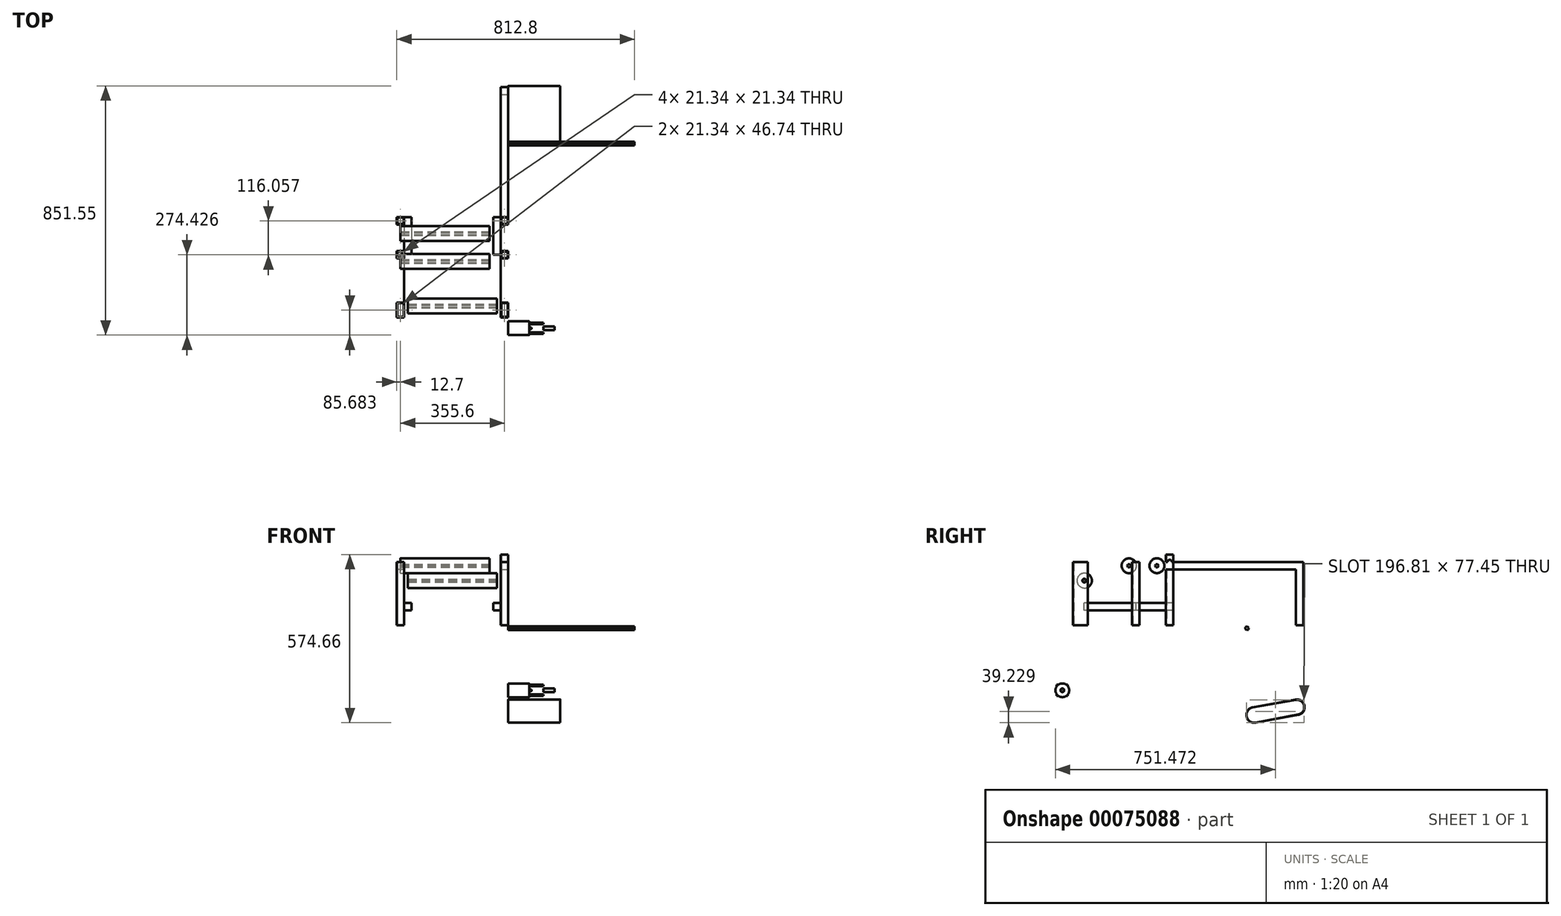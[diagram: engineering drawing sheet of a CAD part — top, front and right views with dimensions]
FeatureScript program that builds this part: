
annotation { "Feature Type Name" : "Feature", "Feature Type Description" : "" }
export const myFeature = defineFeature(function(context is Context, id is Id, definition is map)
    precondition{}
    {
        {
            var Q0;
            Q0=qCreatedBy(makeId("Right.planeOp"),FACE);
            var sketch = newSketch(context, id + "F0", { "sketchPlane" : qUnion([Q0])});
            skLineSegment(sketch, "E0.left", {"start": v(-485.15, -12.17) * mm, "end": v(-485.15, -62.97) * mm, "construction": true});
            skLineSegment(sketch, "E1", {"start": v(-472.45, -12.17) * mm, "end": v(-472.45, 203.73) * mm});
            skLineSegment(sketch, "E2", {"start": v(-472.45, 203.73) * mm, "end": v(-421.65, 203.73) * mm});
            skLineSegment(sketch, "E3", {"start": v(-421.65, 203.73) * mm, "end": v(-421.65, -12.17) * mm});
            skLineSegment(sketch, "E4", {"start": v(-421.65, -12.17) * mm, "end": v(-472.45, -12.17) * mm});
            skLineSegment(sketch, "E5.bottom", {"start": v(-154.95, -12.17) * mm, "end": v(-129.55, -12.17) * mm});
            skLineSegment(sketch, "E5.top", {"start": v(-154.95, 229.13) * mm, "end": v(-129.55, 229.13) * mm});
            skLineSegment(sketch, "E5.left", {"start": v(-154.95, -12.17) * mm, "end": v(-154.95, 229.13) * mm});
            skLineSegment(sketch, "E5.right", {"start": v(-129.55, -12.17) * mm, "end": v(-129.55, 229.13) * mm});
            skLineSegment(sketch, "E6", {"start": v(-283.35, -12.17) * mm, "end": v(-283.35, 178.33) * mm, "construction": true});
            skLineSegment(sketch, "E7.bottom", {"start": v(-421.65, 178.33) * mm, "end": v(-154.95, 178.33) * mm});
            skLineSegment(sketch, "E7.top", {"start": v(-421.65, 203.73) * mm, "end": v(-154.95, 203.73) * mm});
            skLineSegment(sketch, "E7.left", {"start": v(-421.65, 178.33) * mm, "end": v(-421.65, 203.73) * mm});
            skLineSegment(sketch, "E7.right", {"start": v(-154.95, 178.33) * mm, "end": v(-154.95, 203.73) * mm});
            skLineSegment(sketch, "E8", {"start": v(-142.25, -12.17) * mm, "end": v(-142.25, 229.13) * mm, "construction": true});
            skPoint(sketch, "E9.endSnap0", {"position": v(-447.05, -12.17) * mm});
            skCircle(sketch, "E10", {"center": v(-434.35, 140.23) * mm, "radius": 6.35 * mm});
            skLineSegment(sketch, "E11", {"start": v(-421.65, 191.03) * mm, "end": v(-154.95, 191.03) * mm, "construction": true});
            skLineSegment(sketch, "E12", {"start": v(-294.65, 140.23) * mm, "end": v(-294.65, 203.73) * mm, "construction": true});
            skLineSegment(sketch, "E13", {"start": v(-294.65, 191.03) * mm, "end": v(-287.4, 197.2) * mm, "construction": true});
            skCircle(sketch, "E14", {"center": v(-294.65, 191.03) * mm, "radius": 9.52 * mm});
            skLineSegment(sketch, "E15.bottom", {"start": v(-154.95, 203.73) * mm, "end": v(314.95, 203.73) * mm});
            skLineSegment(sketch, "E15.top", {"start": v(-154.95, 178.33) * mm, "end": v(314.95, 178.33) * mm});
            skLineSegment(sketch, "E15.left", {"start": v(-154.95, 203.73) * mm, "end": v(-154.95, 178.33) * mm});
            skLineSegment(sketch, "E15.right", {"start": v(314.95, 203.73) * mm, "end": v(314.95, 178.33) * mm});
            skCircle(sketch, "E16", {"center": v(-142.25, 203.73) * mm, "radius": 7.62 * mm});
            skCircle(sketch, "E17", {"center": v(-212.1, 191.03) * mm, "radius": 7.62 * mm});
            skLineSegment(sketch, "E18.bottom", {"start": v(-271, 203.73) * mm, "end": v(-245.6, 203.73) * mm});
            skLineSegment(sketch, "E18.top", {"start": v(-271, -12.17) * mm, "end": v(-245.6, -12.17) * mm});
            skLineSegment(sketch, "E18.left", {"start": v(-271, 203.73) * mm, "end": v(-271, -12.17) * mm});
            skLineSegment(sketch, "E18.right", {"start": v(-245.6, 203.73) * mm, "end": v(-245.6, -12.17) * mm});
            skLineSegment(sketch, "E19.bottom", {"start": v(314.95, 203.73) * mm, "end": v(289.55, 203.73) * mm});
            skLineSegment(sketch, "E19.top", {"start": v(314.95, -12.17) * mm, "end": v(289.55, -12.17) * mm});
            skLineSegment(sketch, "E19.left", {"start": v(314.95, 203.73) * mm, "end": v(314.95, -12.17) * mm});
            skLineSegment(sketch, "E19.right", {"start": v(289.55, 203.73) * mm, "end": v(289.55, -12.17) * mm});
            skSolve(sketch);
        }
        {
            var Q0;
            Q0=qCreatedBy(makeId("Right.planeOp"),FACE);
            var Q1;
            Q1=qBodyType(qCreatedBy(id+"F2",EDGE),BodyType.WIRE);
            cPlane(context, id + "F1", {"entities" : qUnion([Q0, Q1]), "cplaneType" : CPlaneType.OFFSET, "offset" : 63.5 * mm, "oppositeDirection" : true, "width" : 152.4 * mm, "height" : 152.4 * mm});
        }
        {
            var Q0;
            Q0=qCreatedBy(id+"F1.planeOp",FACE);
            var sketch = newSketch(context, id + "F2", { "sketchPlane" : qUnion([Q0])});
            skCircle(sketch, "E20", {"center": v(-433.76, 140.23) * mm, "radius": 25.4 * mm});
            skCircle(sketch, "E21", {"center": v(-186.1, 191.03) * mm, "radius": 25.4 * mm});
            skCircle(sketch, "E22", {"center": v(-281.36, 191.03) * mm, "radius": 25.4 * mm});
            skCircle(sketch, "E23.cCircle", {"center": v(-433.76, 140.23) * mm, "radius": 5.5 * mm, "construction": true});
            skLineSegment(sketch, "E23.0", {"start": v(-430.58, 134.73) * mm, "end": v(-436.93, 134.73) * mm});
            skLineSegment(sketch, "E23.1", {"start": v(-436.93, 134.73) * mm, "end": v(-440.1, 140.23) * mm});
            skLineSegment(sketch, "E23.2", {"start": v(-440.1, 140.23) * mm, "end": v(-436.93, 145.72) * mm});
            skLineSegment(sketch, "E23.3", {"start": v(-436.93, 145.72) * mm, "end": v(-430.58, 145.72) * mm});
            skLineSegment(sketch, "E23.4", {"start": v(-430.58, 145.72) * mm, "end": v(-427.4, 140.23) * mm});
            skLineSegment(sketch, "E23.5", {"start": v(-427.4, 140.23) * mm, "end": v(-430.58, 134.73) * mm});
            skPoint(sketch, "E23.0.midPoint", {"position": v(-433.76, 134.73) * mm});
            skCircle(sketch, "E24.cCircle", {"center": v(-281.36, 191.03) * mm, "radius": 5.5 * mm, "construction": true});
            skLineSegment(sketch, "E24.0", {"start": v(-278.18, 185.53) * mm, "end": v(-284.53, 185.53) * mm});
            skLineSegment(sketch, "E24.1", {"start": v(-284.53, 185.53) * mm, "end": v(-287.7, 191.03) * mm});
            skLineSegment(sketch, "E24.2", {"start": v(-287.7, 191.03) * mm, "end": v(-284.53, 196.52) * mm});
            skLineSegment(sketch, "E24.3", {"start": v(-284.53, 196.52) * mm, "end": v(-278.18, 196.52) * mm});
            skLineSegment(sketch, "E24.4", {"start": v(-278.18, 196.52) * mm, "end": v(-275, 191.03) * mm});
            skLineSegment(sketch, "E24.5", {"start": v(-275, 191.03) * mm, "end": v(-278.18, 185.53) * mm});
            skPoint(sketch, "E24.0.midPoint", {"position": v(-281.36, 185.53) * mm});
            skCircle(sketch, "E25.cCircle", {"center": v(-186.1, 191.03) * mm, "radius": 5.5 * mm, "construction": true});
            skLineSegment(sketch, "E25.0", {"start": v(-182.93, 185.53) * mm, "end": v(-189.28, 185.53) * mm});
            skLineSegment(sketch, "E25.1", {"start": v(-189.28, 185.53) * mm, "end": v(-192.46, 191.03) * mm});
            skLineSegment(sketch, "E25.2", {"start": v(-192.46, 191.03) * mm, "end": v(-189.28, 196.52) * mm});
            skLineSegment(sketch, "E25.3", {"start": v(-189.28, 196.52) * mm, "end": v(-182.93, 196.52) * mm});
            skLineSegment(sketch, "E25.4", {"start": v(-182.93, 196.52) * mm, "end": v(-179.76, 191.03) * mm});
            skLineSegment(sketch, "E25.5", {"start": v(-179.76, 191.03) * mm, "end": v(-182.93, 185.53) * mm});
            skPoint(sketch, "E25.0.midPoint", {"position": v(-186.1, 185.53) * mm});
            skSolve(sketch);
        }
        {
            var Q0;
            Q0=makeQuery(id+"F2.imprint","IMPRINT",FACE,{"disambiguationData":[TD([[makeQuery(id+"F2.imprint","IMPRINT",EDGE,{"derivedFrom":sQuery(id+"F2.wireOp",EDGE,"E22")}),1.0]])]});
            var Q1;
            Q1=makeQuery(id+"F2.imprint","IMPRINT",FACE,{"disambiguationData":[TD([[makeQuery(id+"F2.imprint","IMPRINT",EDGE,{"derivedFrom":sQuery(id+"F2.wireOp",EDGE,"E21")}),1.0]])]});
            extrude(context, id + "F3", {"entities" : qUnion([Q0, Q1]), "oppositeDirection" : true, "depth" : 304.8 * mm});
        }
        {
            var Q0;
            Q0=makeQuery(id+"F0.imprint","IMPRINT",FACE,{"disambiguationData":[TD([[makeQuery(id+"F0.imprint","IMPRINT",EDGE,{"derivedFrom":sQuery(id+"F0.wireOp",EDGE,"E7.bottom")}),1.0]])]});
            var Q1;
            {var subQ3=sQuery(id+"F0.wireOp",EDGE,"E5.bottom");Q1=makeQuery(id+"F0.imprint","IMPRINT",FACE,{"disambiguationData":[TD([[makeQuery(id+"F0.imprint","IMPRINT",EDGE,{"derivedFrom":subQ3}),1.0]])]});}
            var Q2;
            Q2=makeQuery(id+"F0.imprint","IMPRINT",FACE,{"disambiguationData":[TD([[makeQuery(id+"F0.imprint","IMPRINT",EDGE,{"derivedFrom":sQuery(id+"F0.wireOp",EDGE,"E1")}),-1.0]])]});
            var Q3;
            {var subQ5=sQuery(id+"F0.wireOp",EDGE,"E15.left");Q3=makeQuery(id+"F0.imprint","IMPRINT",FACE,{"disambiguationData":[TD([[makeQuery(id+"F0.imprint","IMPRINT",EDGE,{"derivedFrom":subQ5}),1.0]])]});}
            var Q4;
            {var subQ0=sQuery(id+"F0.wireOp",EDGE,"E5.top");Q4=makeQuery(id+"F0.imprint","IMPRINT",FACE,{"disambiguationData":[TD([[makeQuery(id+"F0.imprint","IMPRINT",EDGE,{"derivedFrom":subQ0}),-1.0]])]});}
            var Q5;
            {var subQ5=sQuery(id+"F0.wireOp",EDGE,"E15.right");Q5=makeQuery(id+"F0.imprint","IMPRINT",FACE,{"disambiguationData":[TD([[makeQuery(id+"F0.imprint","IMPRINT",EDGE,{"derivedFrom":subQ5}),-1.0]])]});}
            var Q6;
            {var subQ0=sQuery(id+"F0.wireOp",EDGE,"E7.left");Q6=makeQuery(id+"F0.imprint","IMPRINT",FACE,{"disambiguationData":[TD([[makeQuery(id+"F0.imprint","IMPRINT",EDGE,{"derivedFrom":subQ0}),-1.0]])]});}
            var Q7;
            {var subQ5=sQuery(id+"F0.wireOp",EDGE,"E18.top");Q7=makeQuery(id+"F0.imprint","IMPRINT",FACE,{"disambiguationData":[TD([[makeQuery(id+"F0.imprint","IMPRINT",EDGE,{"derivedFrom":subQ5}),1.0]])]});}
            var Q8;
            {var subQ0=sQuery(id+"F0.wireOp",EDGE,"E15.left");Q8=makeQuery(id+"F0.imprint","IMPRINT",FACE,{"disambiguationData":[TD([[makeQuery(id+"F0.imprint","IMPRINT",EDGE,{"derivedFrom":subQ0}),-1.0]])]});}
            var Q9;
            {var subQ5=sQuery(id+"F0.wireOp",EDGE,"E19.bottom");Q9=makeQuery(id+"F0.imprint","IMPRINT",FACE,{"disambiguationData":[TD([[makeQuery(id+"F0.imprint","IMPRINT",EDGE,{"derivedFrom":subQ5}),1.0]])]});}
            var Q10;
            {var subQ0=sQuery(id+"F0.wireOp",EDGE,"E15.top");var subQ1=sQuery(id+"F0.wireOp",EDGE,"E5.right");var subQ2=makeQuery(id+"F0.imprint","INTERSECT",VERTEX,{"derivedFrom":[subQ1,subQ0]});Q10=makeQuery(id+"F0.imprint","IMPRINT",FACE,{"disambiguationData":[TD([[makeQuery(id+"F0.imprint","IMPRINT",EDGE,{"disambiguationData":[TD([[subQ2,-1.0]])],"derivedFrom":subQ1}),-1.0]])]});}
            var Q11;
            {var subQ5=sQuery(id+"F0.wireOp",EDGE,"E19.top");Q11=makeQuery(id+"F0.imprint","IMPRINT",FACE,{"disambiguationData":[TD([[makeQuery(id+"F0.imprint","IMPRINT",EDGE,{"derivedFrom":subQ5}),-1.0]])]});}
            extrude(context, id + "F4", {"entities" : qUnion([Q0, Q1, Q2, Q3, Q4, Q5, Q6, Q7, Q8, Q9, Q10, Q11]), "oppositeDirection" : true, "depth" : 25.4 * mm});
        }
        {
            var Q0;
            Q0=makeQuery(id+"F0.imprint","IMPRINT",FACE,{"disambiguationData":[TD([[makeQuery(id+"F0.imprint","IMPRINT",EDGE,{"derivedFrom":sQuery(id+"F0.wireOp",EDGE,"E1")}),-1.0]])]});
            cPlane(context, id + "F5", {"entities" : qUnion([Q0]), "cplaneType" : CPlaneType.OFFSET, "offset" : 190.5 * mm, "oppositeDirection" : true, "width" : 152.4 * mm, "height" : 152.4 * mm});
        }
        {
            var Q0;
            Q0=makeQuery(id+"F2.imprint","IMPRINT",FACE,{"disambiguationData":[TD([[makeQuery(id+"F2.imprint","IMPRINT",EDGE,{"derivedFrom":sQuery(id+"F2.wireOp",EDGE,"E20")}),1.0]])]});
            extrude(context, id + "F6", {"entities" : qUnion([Q0]), "oppositeDirection" : true, "depth" : 279.4 * mm});
        }
        {
            var Q0;
            Q0=makeQuery(id+"F2.imprint","IMPRINT",FACE,{"disambiguationData":[TD([[makeQuery(id+"F2.imprint","IMPRINT",EDGE,{"derivedFrom":sQuery(id+"F2.wireOp",EDGE,"E20")}),1.0]])]});
            extrude(context, id + "F7", {"entities" : qUnion([Q0]), "operationType" : NewBodyOperationType.ADD, "depth" : 25.4 * mm});
        }
        {
            var Q0;
            Q0=qCreatedBy(makeId("Right.planeOp"),FACE);
            var sketch = newSketch(context, id + "F8", { "sketchPlane" : qUnion([Q0])});
            skCircle(sketch, "E26.cCircle", {"center": v(121.57, -22.95) * mm, "radius": 5.5 * mm, "construction": true});
            skLineSegment(sketch, "E26.0", {"start": v(126.52, -26.93) * mm, "end": v(120.6, -29.23) * mm});
            skLineSegment(sketch, "E26.1", {"start": v(120.6, -29.23) * mm, "end": v(115.65, -25.26) * mm});
            skLineSegment(sketch, "E26.2", {"start": v(115.65, -25.26) * mm, "end": v(116.61, -18.98) * mm});
            skLineSegment(sketch, "E26.3", {"start": v(116.61, -18.98) * mm, "end": v(122.53, -16.68) * mm});
            skLineSegment(sketch, "E26.4", {"start": v(122.53, -16.68) * mm, "end": v(127.48, -20.65) * mm});
            skLineSegment(sketch, "E26.5", {"start": v(127.48, -20.65) * mm, "end": v(126.52, -26.93) * mm});
            skPoint(sketch, "E26.0.midPoint", {"position": v(123.56, -28.08) * mm});
            skSolve(sketch);
        }
        {
            var Q0;
            Q0=makeQuery(id+"F8.imprint","IMPRINT",FACE,{"disambiguationData":[TD([[makeQuery(id+"F8.imprint","IMPRINT",EDGE,{"derivedFrom":sQuery(id+"F8.wireOp",EDGE,"E26.0")}),-1.0]])]});
            extrude(context, id + "F9", {"entities" : qUnion([Q0]), "depth" : 431.8 * mm});
        }
        {
            var Q0;
            Q0=makeQuery(id+"F4.opExtrude","CAP_FACE",FACE,{"disambiguationData":[OSD([sQuery(id+"F0.wireOp",EDGE,"E1"),sQuery(id+"F0.wireOp",EDGE,"E2"),sQuery(id+"F0.wireOp",EDGE,"E3"),sQuery(id+"F0.wireOp",EDGE,"E4"),sQuery(id+"F0.wireOp",EDGE,"E5.bottom"),sQuery(id+"F0.wireOp",EDGE,"E5.top"),sQuery(id+"F0.wireOp",EDGE,"E5.left"),sQuery(id+"F0.wireOp",EDGE,"E5.right"),sQuery(id+"F0.wireOp",EDGE,"E7.bottom"),sQuery(id+"F0.wireOp",EDGE,"E7.top"),sQuery(id+"F0.wireOp",EDGE,"E10"),sQuery(id+"F0.wireOp",EDGE,"E14"),sQuery(id+"F0.wireOp",EDGE,"E15.bottom"),sQuery(id+"F0.wireOp",EDGE,"E15.top"),sQuery(id+"F0.wireOp",EDGE,"E15.right"),sQuery(id+"F0.wireOp",EDGE,"E16"),sQuery(id+"F0.wireOp",EDGE,"E17"),sQuery(id+"F0.wireOp",EDGE,"E18.bottom"),sQuery(id+"F0.wireOp",EDGE,"E18.top"),sQuery(id+"F0.wireOp",EDGE,"E18.left"),sQuery(id+"F0.wireOp",EDGE,"E18.right")])],"isStart":false});
            var sketch = newSketch(context, id + "F10", { "sketchPlane" : qUnion([Q0])});
            skLineSegment(sketch, "E27.bottom", {"start": v(129.55, 64.03) * mm, "end": v(258.3, 64.03) * mm});
            skLineSegment(sketch, "E27.top", {"start": v(129.55, 38.63) * mm, "end": v(258.3, 38.63) * mm});
            skLineSegment(sketch, "E27.left", {"start": v(129.55, 64.03) * mm, "end": v(129.55, 38.63) * mm});
            skLineSegment(sketch, "E27.right", {"start": v(258.3, 64.03) * mm, "end": v(258.3, 38.63) * mm});
            skSolve(sketch);
        }
        {
            var Q0;
            {var subQ4=makeQuery(id+"F4.opExtrude","CAP_EDGE",EDGE,{"disambiguationData":[OSD([sQuery(id+"F0.wireOp",EDGE,"E18.right")])],"isStart":false});var subQ6=sQuery(id+"F10.wireOp",EDGE,"E27.top");var subQ8=makeQuery(id+"F10.imprint","INTERSECT",VERTEX,{"derivedFrom":[subQ4,subQ6]});Q0=makeQuery(id+"F10.imprint","IMPRINT",FACE,{"disambiguationData":[TD([[makeQuery(id+"F10.imprint","IMPRINT",EDGE,{"disambiguationData":[TD([[subQ8,1.0]])],"derivedFrom":subQ4}),-1.0]])]});}
            var Q1;
            {var subQ0=sQuery(id+"F10.wireOp",EDGE,"E27.left");Q1=makeQuery(id+"F10.imprint","IMPRINT",FACE,{"disambiguationData":[TD([[makeQuery(id+"F10.imprint","IMPRINT",EDGE,{"derivedFrom":subQ0}),-1.0]])]});}
            var Q2;
            {var subQ0=sQuery(id+"F10.wireOp",EDGE,"E27.right");Q2=makeQuery(id+"F10.imprint","IMPRINT",FACE,{"disambiguationData":[TD([[makeQuery(id+"F10.imprint","IMPRINT",EDGE,{"derivedFrom":subQ0}),-1.0]])]});}
            extrude(context, id + "F11", {"entities" : qUnion([Q0, Q1, Q2]), "operationType" : NewBodyOperationType.ADD, "depth" : 25.4 * mm});
        }
        {
            var Q0;
            {var subQ0=sQuery(id+"F0.wireOp",EDGE,"E17");var subQ1=sQuery(id+"F0.wireOp",EDGE,"E5.right");var subQ2=sQuery(id+"F0.wireOp",EDGE,"E5.top");var subQ3=sQuery(id+"F0.wireOp",EDGE,"E15.bottom");var subQ4=sQuery(id+"F0.wireOp",EDGE,"E16");var subQ5=sQuery(id+"F0.wireOp",EDGE,"E5.bottom");var subQ6=sQuery(id+"F0.wireOp",EDGE,"E15.top");var subQ7=sQuery(id+"F0.wireOp",EDGE,"E15.right");var subQ8=sQuery(id+"F0.wireOp",EDGE,"E5.left");var subQ10=sQuery(id+"F0.wireOp",EDGE,"E7.top");var subQ11=sQuery(id+"F0.wireOp",EDGE,"E7.bottom");var subQ13=sQuery(id+"F0.wireOp",EDGE,"E14");var subQ14=sQuery(id+"F0.wireOp",EDGE,"E18.right");var subQ15=sQuery(id+"F0.wireOp",EDGE,"E18.left");var subQ16=sQuery(id+"F0.wireOp",EDGE,"E4");var subQ17=sQuery(id+"F0.wireOp",EDGE,"E3");var subQ18=sQuery(id+"F0.wireOp",EDGE,"E18.bottom");var subQ19=sQuery(id+"F0.wireOp",EDGE,"E2");var subQ20=sQuery(id+"F0.wireOp",EDGE,"E18.top");var subQ21=sQuery(id+"F0.wireOp",EDGE,"E10");var subQ22=sQuery(id+"F0.wireOp",EDGE,"E1");Q0=makeQuery(id+"F11.boolean.opBoolean","SPLIT",FACE,{"disambiguationData":[TD([makeQuery(id+"F4.opExtrude","SWEPT_FACE",FACE,{"disambiguationData":[OSD([subQ22])]})])],"derivedFrom":makeQuery(id+"F4.opExtrude","CAP_FACE",FACE,{"disambiguationData":[OSD([subQ22,subQ19,subQ17,subQ16,subQ5,subQ2,subQ8,subQ1,subQ11,subQ10,subQ21,subQ13,subQ3,subQ6,subQ7,subQ4,subQ0,subQ18,subQ20,subQ15,subQ14])],"isStart":false})});}
            var sketch = newSketch(context, id + "F12", { "sketchPlane" : qUnion([Q0])});
            skLineSegment(sketch, "E28.bottom", {"start": v(258.3, 38.63) * mm, "end": v(434.35, 38.63) * mm});
            skLineSegment(sketch, "E28.top", {"start": v(258.3, 64.03) * mm, "end": v(434.35, 64.03) * mm});
            skLineSegment(sketch, "E28.left", {"start": v(258.3, 38.63) * mm, "end": v(258.3, 64.03) * mm});
            skLineSegment(sketch, "E28.right", {"start": v(434.35, 38.63) * mm, "end": v(434.35, 64.03) * mm});
            skSolve(sketch);
        }
        {
            var Q0;
            {var subQ0=sQuery(id+"F12.wireOp",EDGE,"E28.bottom");var subQ1=makeQuery(id+"F4.opExtrude","CAP_EDGE",EDGE,{"disambiguationData":[OSD([sQuery(id+"F0.wireOp",EDGE,"E18.left")])],"isStart":false});var subQ2=makeQuery(id+"F12.imprint","INTERSECT",VERTEX,{"derivedFrom":[subQ1,subQ0]});Q0=makeQuery(id+"F12.imprint","IMPRINT",FACE,{"disambiguationData":[TD([[makeQuery(id+"F12.imprint","IMPRINT",EDGE,{"disambiguationData":[TD([[subQ2,-1.0]])],"derivedFrom":subQ0}),1.0]])]});}
            var Q1;
            {var subQ0=sQuery(id+"F12.wireOp",EDGE,"E28.right");Q1=makeQuery(id+"F12.imprint","IMPRINT",FACE,{"disambiguationData":[TD([[makeQuery(id+"F12.imprint","IMPRINT",EDGE,{"derivedFrom":subQ0}),1.0]])]});}
            var Q2;
            {var subQ0=sQuery(id+"F12.wireOp",EDGE,"E28.left");Q2=makeQuery(id+"F12.imprint","IMPRINT",FACE,{"disambiguationData":[TD([[makeQuery(id+"F12.imprint","IMPRINT",EDGE,{"derivedFrom":subQ0}),1.0]])]});}
            extrude(context, id + "F13", {"entities" : qUnion([Q0, Q1, Q2]), "operationType" : NewBodyOperationType.ADD, "depth" : 1 / 203.2 * mm});
        }
        {
            var Q0;
            Q0=makeQuery(id+"F4.opExtrude","SWEPT_FACE",FACE,{"disambiguationData":[OSD([sQuery(id+"F0.wireOp",EDGE,"E5.bottom")])]});
            var sketch = newSketch(context, id + "F14", { "sketchPlane" : qUnion([Q0])});
            skLineSegment(sketch, "E29.bottom", {"start": v(-23.37, 152.91) * mm, "end": v(-2.03, 152.91) * mm});
            skLineSegment(sketch, "E29.top", {"start": v(-23.37, 131.58) * mm, "end": v(-2.03, 131.58) * mm});
            skLineSegment(sketch, "E29.left", {"start": v(-23.37, 152.91) * mm, "end": v(-23.37, 131.58) * mm});
            skLineSegment(sketch, "E29.right", {"start": v(-2.03, 152.91) * mm, "end": v(-2.03, 131.58) * mm});
            skSolve(sketch);
        }
        {
            var Q0;
            Q0=makeQuery(id+"F14.imprint","IMPRINT",FACE,{"disambiguationData":[TD([[makeQuery(id+"F14.imprint","IMPRINT",EDGE,{"derivedFrom":sQuery(id+"F14.wireOp",EDGE,"E29.bottom")}),-1.0]])]});
            var Q1;
            Q1=makeQuery(id+"F4.opExtrude","SWEPT_FACE",FACE,{"disambiguationData":[OSD([sQuery(id+"F0.wireOp",EDGE,"E5.top")])]});
            extrude(context, id + "F15", {"entities" : qUnion([Q0]), "operationType" : NewBodyOperationType.REMOVE, "endBound" : BoundingType.UP_TO_SURFACE, "oppositeDirection" : true, "endBoundEntityFace" : qUnion([Q1]), "depth" : 25.4 * mm});
        }
        {
            var Q0;
            Q0=makeQuery(id+"F4.opExtrude","SWEPT_FACE",FACE,{"disambiguationData":[OSD([sQuery(id+"F0.wireOp",EDGE,"E18.top")])]});
            var sketch = newSketch(context, id + "F16", { "sketchPlane" : qUnion([Q0])});
            skLineSegment(sketch, "E30.bottom", {"start": v(-23.37, 268.97) * mm, "end": v(-2.03, 268.97) * mm});
            skLineSegment(sketch, "E30.top", {"start": v(-23.37, 247.64) * mm, "end": v(-2.03, 247.64) * mm});
            skLineSegment(sketch, "E30.left", {"start": v(-23.37, 268.97) * mm, "end": v(-23.37, 247.64) * mm});
            skLineSegment(sketch, "E30.right", {"start": v(-2.03, 268.97) * mm, "end": v(-2.03, 247.64) * mm});
            skSolve(sketch);
        }
        {
            var Q0;
            Q0=makeQuery(id+"F16.imprint","IMPRINT",FACE,{"disambiguationData":[TD([[makeQuery(id+"F16.imprint","IMPRINT",EDGE,{"derivedFrom":sQuery(id+"F16.wireOp",EDGE,"E30.bottom")}),-1.0]])]});
            var Q1;
            Q1=makeQuery(id+"F4.opExtrude","SWEPT_FACE",FACE,{"disambiguationData":[OSD([sQuery(id+"F0.wireOp",EDGE,"E2"),sQuery(id+"F0.wireOp",EDGE,"E7.top"),sQuery(id+"F0.wireOp",EDGE,"E18.bottom")])]});
            extrude(context, id + "F17", {"entities" : qUnion([Q0]), "operationType" : NewBodyOperationType.REMOVE, "endBound" : BoundingType.UP_TO_SURFACE, "oppositeDirection" : true, "endBoundEntityFace" : qUnion([Q1]), "depth" : 25.4 * mm});
        }
        {
            var Q0;
            Q0=makeQuery(id+"F4.opExtrude","SWEPT_FACE",FACE,{"disambiguationData":[OSD([sQuery(id+"F0.wireOp",EDGE,"E4")])]});
            var sketch = newSketch(context, id + "F18", { "sketchPlane" : qUnion([Q0])});
            skLineSegment(sketch, "E31.bottom", {"start": v(-23.37, 470.41) * mm, "end": v(-2.03, 470.41) * mm});
            skLineSegment(sketch, "E31.top", {"start": v(-23.37, 423.68) * mm, "end": v(-2.03, 423.68) * mm});
            skLineSegment(sketch, "E31.left", {"start": v(-23.37, 470.41) * mm, "end": v(-23.37, 423.68) * mm});
            skLineSegment(sketch, "E31.right", {"start": v(-2.03, 470.41) * mm, "end": v(-2.03, 423.68) * mm});
            skSolve(sketch);
        }
        {
            var Q0;
            Q0=makeQuery(id+"F18.imprint","IMPRINT",FACE,{"disambiguationData":[TD([[makeQuery(id+"F18.imprint","IMPRINT",EDGE,{"derivedFrom":sQuery(id+"F18.wireOp",EDGE,"E31.bottom")}),-1.0]])]});
            var Q1;
            Q1=makeQuery(id+"F4.opExtrude","SWEPT_FACE",FACE,{"disambiguationData":[OSD([sQuery(id+"F0.wireOp",EDGE,"E2"),sQuery(id+"F0.wireOp",EDGE,"E7.top"),sQuery(id+"F0.wireOp",EDGE,"E18.bottom")])]});
            extrude(context, id + "F19", {"entities" : qUnion([Q0]), "operationType" : NewBodyOperationType.REMOVE, "endBound" : BoundingType.UP_TO_SURFACE, "oppositeDirection" : true, "endBoundEntityFace" : qUnion([Q1]), "depth" : 25.4 * mm});
        }
        {
            var Q0;
            Q0=makeQuery(id+"F4.opExtrude","SWEPT_BODY",BODY,{"disambiguationData":[OSD([sQuery(id+"F0.wireOp",EDGE,"E1"),sQuery(id+"F0.wireOp",EDGE,"E2"),sQuery(id+"F0.wireOp",EDGE,"E3"),sQuery(id+"F0.wireOp",EDGE,"E4"),sQuery(id+"F0.wireOp",EDGE,"E5.bottom"),sQuery(id+"F0.wireOp",EDGE,"E5.top"),sQuery(id+"F0.wireOp",EDGE,"E5.left"),sQuery(id+"F0.wireOp",EDGE,"E5.right"),sQuery(id+"F0.wireOp",EDGE,"E7.bottom"),sQuery(id+"F0.wireOp",EDGE,"E7.top"),sQuery(id+"F0.wireOp",EDGE,"E10"),sQuery(id+"F0.wireOp",EDGE,"E14")])]});
            var Q1;
            Q1=qCreatedBy(id+"F5.planeOp",FACE);
            mirror(context, id + "F20", {"entities" : qUnion([Q0]), "mirrorPlane" : qUnion([Q1])});
        }
        {
            var Q0;
            Q0=qCreatedBy(makeId("Right.planeOp"),FACE);
            var sketch = newSketch(context, id + "F21", { "sketchPlane" : qUnion([Q0])});
            skArc(sketch, "E32", {"start": v(296.87, -317.57) * mm, "mid": v(317.15, -288.1) * mm, "end": v(287.85, -267.58) * mm});
            skArc(sketch, "E33", {"start": v(142.04, -292.61) * mm, "mid": v(120.33, -323.58) * mm, "end": v(151.49, -345.03) * mm});
            skLineSegment(sketch, "E34", {"start": v(287.85, -267.58) * mm, "end": v(142.04, -292.61) * mm});
            skLineSegment(sketch, "E35", {"start": v(151.49, -345.03) * mm, "end": v(296.87, -317.57) * mm});
            skLineSegment(sketch, "E36", {"start": v(151.27, -345.1) * mm, "end": v(296.88, -318.86) * mm});
            skLineSegment(sketch, "E37", {"start": v(287.42, -266.36) * mm, "end": v(141.81, -292.61) * mm});
            skArc(sketch, "E38", {"start": v(141.81, -292.61) * mm, "mid": v(120.3, -323.59) * mm, "end": v(151.27, -345.1) * mm});
            skArc(sketch, "E39", {"start": v(296.88, -318.86) * mm, "mid": v(318.4, -287.88) * mm, "end": v(287.42, -266.36) * mm});
            skSolve(sketch);
        }
        {
            var Q0;
            Q0=makeQuery(id+"F21.imprint","IMPRINT",FACE,{"disambiguationData":[TD([[makeQuery(id+"F21.imprint","IMPRINT",EDGE,{"derivedFrom":sQuery(id+"F21.wireOp",EDGE,"E32")}),-1.0]])]});
            extrude(context, id + "F22", {"entities" : qUnion([Q0]), "depth" : 177.8 * mm});
        }
        {
            var Q0;
            Q0=qCreatedBy(makeId("Right.planeOp"),FACE);
            var sketch = newSketch(context, id + "F23", { "sketchPlane" : qUnion([Q0])});
            skCircle(sketch, "E40", {"center": v(-509.23, -234.63) * mm, "radius": 23.5 * mm});
            skSolve(sketch);
        }
        {
            var Q0;
            Q0=makeQuery(id+"F23.imprint","IMPRINT",FACE,{"disambiguationData":[TD([[makeQuery(id+"F23.imprint","IMPRINT",EDGE,{"derivedFrom":sQuery(id+"F23.wireOp",EDGE,"E40")}),1.0]])]});
            extrude(context, id + "F24", {"entities" : qUnion([Q0]), "depth" : 71.37 * mm});
        }
        {
            var Q0;
            Q0=makeQuery(id+"F24.opExtrude","CAP_FACE",FACE,{"disambiguationData":[OSD([sQuery(id+"F23.wireOp",EDGE,"E40")])],"isStart":false});
            var sketch = newSketch(context, id + "F25", { "sketchPlane" : qUnion([Q0])});
            skCircle(sketch, "E41", {"center": v(-509.23, -234.63) * mm, "radius": 2.5 * mm});
            skSolve(sketch);
        }
        {
            var Q0;
            Q0=makeQuery(id+"F25.imprint","IMPRINT",FACE,{"disambiguationData":[TD([[makeQuery(id+"F25.imprint","IMPRINT",EDGE,{"derivedFrom":sQuery(id+"F25.wireOp",EDGE,"E41")}),1.0]])]});
            extrude(context, id + "F26", {"entities" : qUnion([Q0]), "operationType" : NewBodyOperationType.ADD, "depth" : 7.62 * mm});
        }
        {
            var Q0;
            Q0=makeQuery(id+"F24.opExtrude","CAP_FACE",FACE,{"disambiguationData":[OSD([sQuery(id+"F23.wireOp",EDGE,"E40")])],"isStart":false});
            var sketch = newSketch(context, id + "F27", { "sketchPlane" : qUnion([Q0])});
            skLineSegment(sketch, "E42.bottom", {"start": v(-528.5, -215.54) * mm, "end": v(-490.4, -215.54) * mm});
            skLineSegment(sketch, "E42.top", {"start": v(-528.5, -253.64) * mm, "end": v(-490.4, -253.64) * mm});
            skLineSegment(sketch, "E42.left", {"start": v(-528.5, -215.54) * mm, "end": v(-528.5, -253.64) * mm});
            skLineSegment(sketch, "E42.right", {"start": v(-490.4, -215.54) * mm, "end": v(-490.4, -253.64) * mm});
            skSolve(sketch);
        }
        {
            var Q0;
            Q0=makeQuery(id+"F27.imprint","IMPRINT",FACE,{"disambiguationData":[TD([[makeQuery(id+"F27.imprint","IMPRINT",EDGE,{"derivedFrom":makeQuery(id+"F26.opExtrude","CAP_EDGE",EDGE,{"disambiguationData":[OSD([sQuery(id+"F25.wireOp",EDGE,"E41")])],"isStart":true})}),-1.0]])]});
            var Q1;
            {var subQ0=sQuery(id+"F27.wireOp",EDGE,"E42.left");var subQ1=sQuery(id+"F27.wireOp",EDGE,"E42.bottom");var subQ2=makeQuery(id+"F27.imprint","INTERSECT",VERTEX,{"derivedFrom":[subQ1,subQ0]});Q1=makeQuery(id+"F27.imprint","IMPRINT",FACE,{"disambiguationData":[TD([[makeQuery(id+"F27.imprint","IMPRINT",EDGE,{"disambiguationData":[TD([[subQ2,-1.0]])],"derivedFrom":subQ1}),-1.0]])]});}
            var Q2;
            {var subQ0=sQuery(id+"F27.wireOp",EDGE,"E42.left");var subQ1=sQuery(id+"F27.wireOp",EDGE,"E42.top");var subQ2=makeQuery(id+"F27.imprint","INTERSECT",VERTEX,{"derivedFrom":[subQ1,subQ0]});Q2=makeQuery(id+"F27.imprint","IMPRINT",FACE,{"disambiguationData":[TD([[makeQuery(id+"F27.imprint","IMPRINT",EDGE,{"disambiguationData":[TD([[subQ2,-1.0]])],"derivedFrom":subQ1}),1.0]])]});}
            var Q3;
            {var subQ0=sQuery(id+"F27.wireOp",EDGE,"E42.right");var subQ1=sQuery(id+"F27.wireOp",EDGE,"E42.top");var subQ2=makeQuery(id+"F27.imprint","INTERSECT",VERTEX,{"derivedFrom":[subQ1,subQ0]});Q3=makeQuery(id+"F27.imprint","IMPRINT",FACE,{"disambiguationData":[TD([[makeQuery(id+"F27.imprint","IMPRINT",EDGE,{"disambiguationData":[TD([[subQ2,1.0]])],"derivedFrom":subQ1}),1.0]])]});}
            var Q4;
            {var subQ0=sQuery(id+"F27.wireOp",EDGE,"E42.right");var subQ1=sQuery(id+"F27.wireOp",EDGE,"E42.bottom");var subQ2=makeQuery(id+"F27.imprint","INTERSECT",VERTEX,{"derivedFrom":[subQ1,subQ0]});Q4=makeQuery(id+"F27.imprint","IMPRINT",FACE,{"disambiguationData":[TD([[makeQuery(id+"F27.imprint","IMPRINT",EDGE,{"disambiguationData":[TD([[subQ2,1.0]])],"derivedFrom":subQ1}),-1.0]])]});}
            extrude(context, id + "F28", {"entities" : qUnion([Q0, Q1, Q2, Q3, Q4]), "operationType" : NewBodyOperationType.ADD, "depth" : 48.26 * mm});
        }
        {
            var Q0;
            Q0=makeQuery(id+"F28.opExtrude","CAP_FACE",FACE,{"disambiguationData":[OSD([sQuery(id+"F25.wireOp",EDGE,"E41"),sQuery(id+"F27.wireOp",EDGE,"E42.bottom"),sQuery(id+"F27.wireOp",EDGE,"E42.top"),sQuery(id+"F27.wireOp",EDGE,"E42.left"),sQuery(id+"F27.wireOp",EDGE,"E42.right")])],"isStart":false});
            var sketch = newSketch(context, id + "F29", { "sketchPlane" : qUnion([Q0])});
            skCircle(sketch, "E43", {"center": v(-509.23, -234.63) * mm, "radius": 6.35 * mm});
            skSolve(sketch);
        }
        {
            var Q0;
            Q0=makeQuery(id+"F29.imprint","IMPRINT",FACE,{"disambiguationData":[TD([[makeQuery(id+"F29.imprint","IMPRINT",EDGE,{"derivedFrom":sQuery(id+"F29.wireOp",EDGE,"E43")}),1.0]])]});
            var Q1;
            Q1=makeQuery(id+"F29.imprint","IMPRINT",FACE,{"disambiguationData":[TD([[makeQuery(id+"F29.imprint","IMPRINT",EDGE,{"derivedFrom":makeQuery(id+"F28.opExtrude","CAP_EDGE",EDGE,{"disambiguationData":[OSD([sQuery(id+"F25.wireOp",EDGE,"E41")])],"isStart":false})}),1.0]])]});
            extrude(context, id + "F30", {"entities" : qUnion([Q0, Q1]), "operationType" : NewBodyOperationType.ADD, "depth" : 38.1 * mm});
        }
    });
